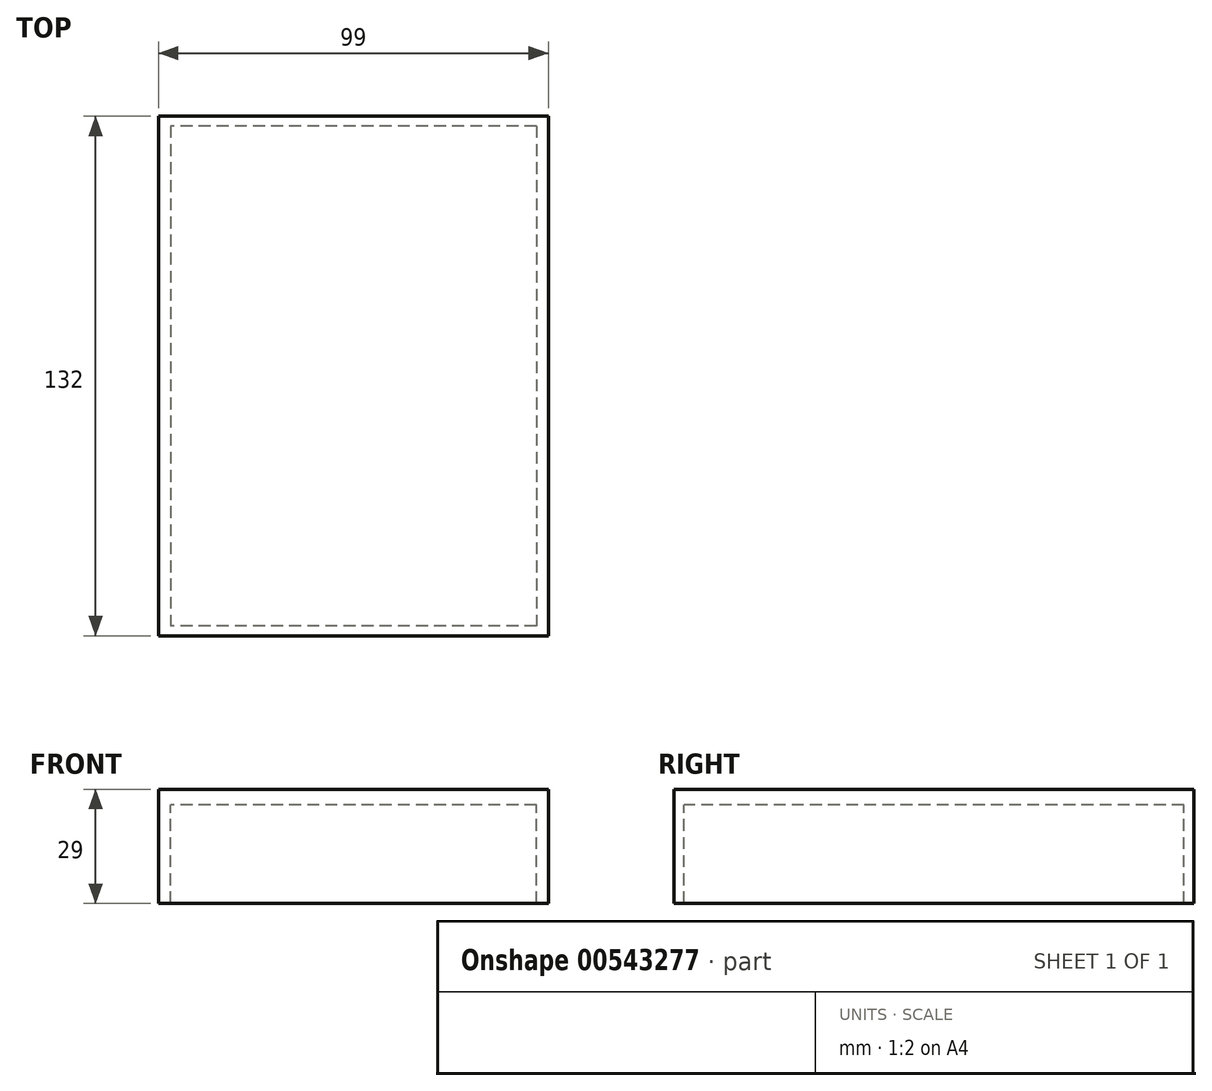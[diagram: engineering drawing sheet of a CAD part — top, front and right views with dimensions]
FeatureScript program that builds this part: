
annotation { "Feature Type Name" : "Feature", "Feature Type Description" : "" }
export const myFeature = defineFeature(function(context is Context, id is Id, definition is map)
    precondition{}
    {
        {
            var Q0;
            Q0=qCreatedBy(makeId("Top.planeOp"),FACE);
            var sketch = newSketch(context, id + "F0", { "sketchPlane" : qUnion([Q0])});
            skLineSegment(sketch, "E0.bottom", {"start": v(49.5, -66) * mm, "end": v(-49.5, -66) * mm});
            skLineSegment(sketch, "E0.top", {"start": v(49.5, 66) * mm, "end": v(-49.5, 66) * mm});
            skLineSegment(sketch, "E0.left", {"start": v(49.5, -66) * mm, "end": v(49.5, 66) * mm});
            skLineSegment(sketch, "E0.right", {"start": v(-49.5, -66) * mm, "end": v(-49.5, 66) * mm});
            skPoint(sketch, "E0.middle", {"position": v(0, 0) * mm});
            skSolve(sketch);
        }
        {
            var Q0;
            Q0=makeQuery(id+"F0.imprint","IMPRINT",FACE,{"disambiguationData":[TD([[makeQuery(id+"F0.imprint","IMPRINT",EDGE,{"derivedFrom":sQuery(id+"F0.wireOp",EDGE,"E0.bottom")}),-1.0]])]});
            extrude(context, id + "F1", {"entities" : qUnion([Q0]), "depth" : 4 * mm, "offsetDistance" : 25 * mm});
        }
        {
            var Q0;
            Q0=makeQuery(id+"F1.opExtrude","CAP_FACE",FACE,{"disambiguationData":[OSD([sQuery(id+"F0.wireOp",EDGE,"E0.bottom"),sQuery(id+"F0.wireOp",EDGE,"E0.top"),sQuery(id+"F0.wireOp",EDGE,"E0.left"),sQuery(id+"F0.wireOp",EDGE,"E0.right")])],"isStart":true});
            var sketch = newSketch(context, id + "F2", { "sketchPlane" : qUnion([Q0])});
            skLineSegment(sketch, "E1.bottom", {"start": v(46.5, -63.5) * mm, "end": v(-46.5, -63.5) * mm});
            skLineSegment(sketch, "E1.top", {"start": v(46.5, 63.5) * mm, "end": v(-46.5, 63.5) * mm});
            skLineSegment(sketch, "E1.left", {"start": v(46.5, -63.5) * mm, "end": v(46.5, 63.5) * mm});
            skLineSegment(sketch, "E1.right", {"start": v(-46.5, -63.5) * mm, "end": v(-46.5, 63.5) * mm});
            skPoint(sketch, "E1.middle", {"position": v(0, 0) * mm});
            skSolve(sketch);
        }
        {
            var Q0;
            Q0=makeQuery(id+"F2.imprint","IMPRINT",FACE,{"disambiguationData":[TD([[makeQuery(id+"F2.imprint","IMPRINT",EDGE,{"derivedFrom":sQuery(id+"F2.wireOp",EDGE,"E1.bottom")}),1.0]])]});
            extrude(context, id + "F3", {"entities" : qUnion([Q0]), "operationType" : NewBodyOperationType.ADD, "depth" : 25 * mm, "offsetDistance" : 25 * mm});
        }
    });
